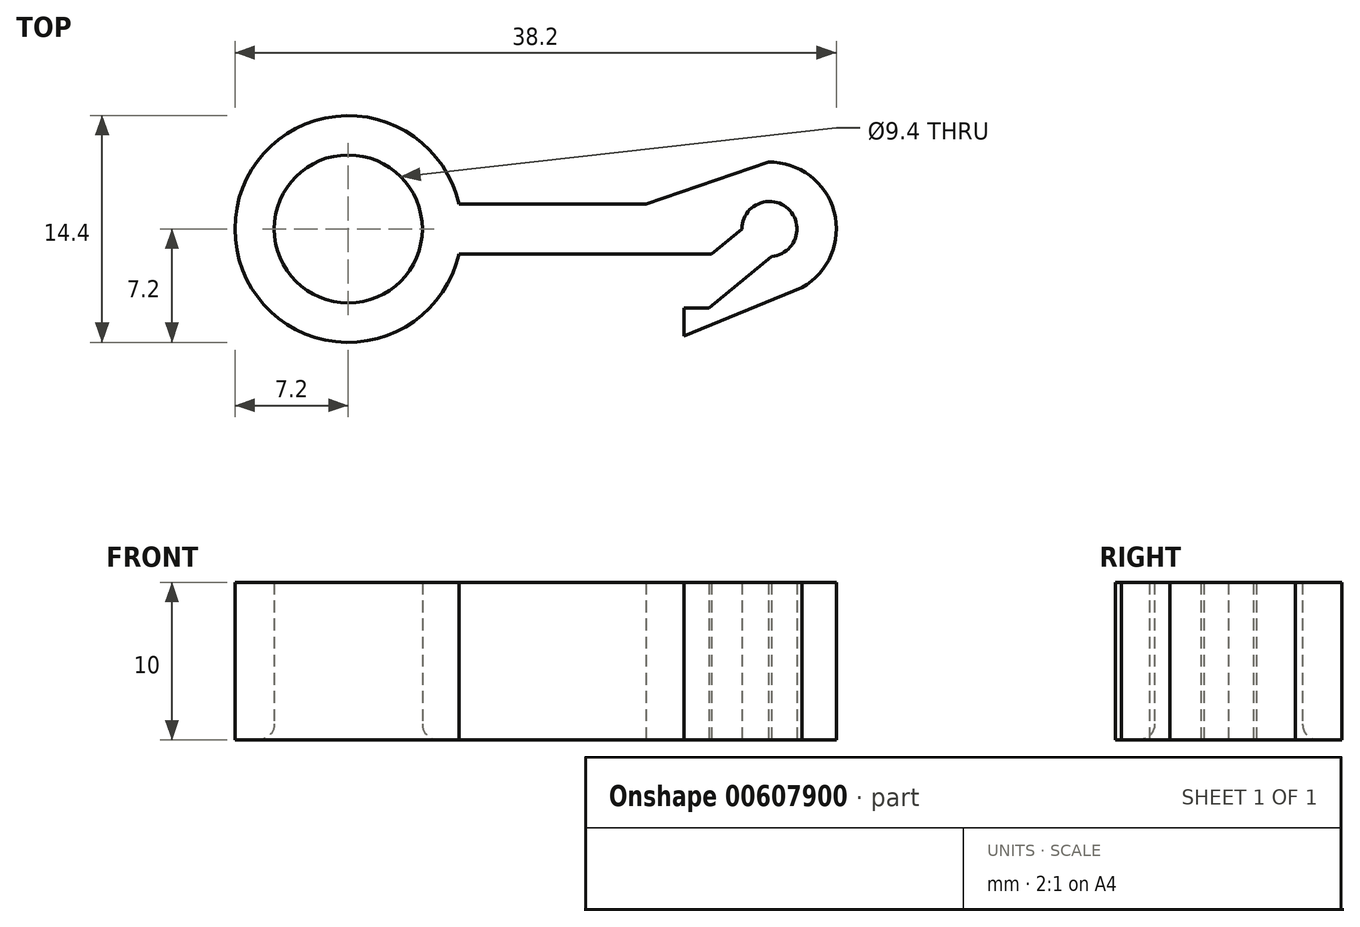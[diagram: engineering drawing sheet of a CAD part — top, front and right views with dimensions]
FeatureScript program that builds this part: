
annotation { "Feature Type Name" : "Feature", "Feature Type Description" : "" }
export const myFeature = defineFeature(function(context is Context, id is Id, definition is map)
    precondition{}
    {
        {
            var Q0;
            Q0=qCreatedBy(makeId("Top.planeOp"),FACE);
            var sketch = newSketch(context, id + "F0", { "sketchPlane" : qUnion([Q0])});
            skCircle(sketch, "E0", {"center": v(0, 0) * mm, "radius": 4.7 * mm});
            skCircle(sketch, "E1", {"center": v(0, 0) * mm, "radius": 7.2 * mm});
            skLineSegment(sketch, "E2.bottom", {"start": v(25, 1.58) * mm, "end": v(-25, 1.58) * mm});
            skLineSegment(sketch, "E2.top", {"start": v(25, -1.58) * mm, "end": v(-25, -1.58) * mm});
            skLineSegment(sketch, "E2.left", {"start": v(25, 1.58) * mm, "end": v(25, -1.58) * mm});
            skLineSegment(sketch, "E2.right", {"start": v(-25, 1.58) * mm, "end": v(-25, -1.58) * mm});
            skCircle(sketch, "E3", {"center": v(26.75, 0) * mm, "radius": 4.25 * mm});
            skCircle(sketch, "E4", {"center": v(26.75, 0) * mm, "radius": 1.75 * mm});
            skLineSegment(sketch, "E5", {"start": v(26.69, 4.25) * mm, "end": v(18.9, 1.58) * mm});
            skLineSegment(sketch, "E6", {"start": v(25, 0) * mm, "end": v(21.76, -2.63) * mm});
            skLineSegment(sketch, "E7", {"start": v(26.88, -1.74) * mm, "end": v(22.9, -5.03) * mm});
            skLineSegment(sketch, "E8", {"start": v(22.9, -5.03) * mm, "end": v(21.32, -5.03) * mm});
            skLineSegment(sketch, "E9", {"start": v(21.32, -5.03) * mm, "end": v(21.32, -6.8) * mm});
            skLineSegment(sketch, "E10", {"start": v(21.32, -6.8) * mm, "end": v(28.82, -3.71) * mm});
            skSolve(sketch);
        }
        {
            var Q0;
            {var subQ0=sQuery(id+"F0.wireOp",EDGE,"E2.bottom");var subQ1=sQuery(id+"F0.wireOp",EDGE,"E0");var subQ2=makeQuery(id+"F0.imprint","INTERSECT",VERTEX,{"disambiguationData":[OD(0.0)],"derivedFrom":[subQ1,subQ0]});Q0=makeQuery(id+"F0.imprint","IMPRINT",FACE,{"disambiguationData":[TD([[makeQuery(id+"F0.imprint","IMPRINT",EDGE,{"disambiguationData":[TD([[subQ2,1.0]])],"derivedFrom":subQ1}),-1.0]])]});}
            var Q1;
            {var subQ0=sQuery(id+"F0.wireOp",EDGE,"E2.bottom");var subQ1=sQuery(id+"F0.wireOp",EDGE,"E0");var subQ2=makeQuery(id+"F0.imprint","INTERSECT",VERTEX,{"disambiguationData":[OD(0.0)],"derivedFrom":[subQ1,subQ0]});Q1=makeQuery(id+"F0.imprint","IMPRINT",FACE,{"disambiguationData":[TD([[makeQuery(id+"F0.imprint","IMPRINT",EDGE,{"disambiguationData":[TD([[subQ2,-1.0]])],"derivedFrom":subQ1}),-1.0]])]});}
            var Q2;
            {var subQ0=sQuery(id+"F0.wireOp",EDGE,"E2.top");var subQ1=sQuery(id+"F0.wireOp",EDGE,"E0");var subQ2=makeQuery(id+"F0.imprint","INTERSECT",VERTEX,{"disambiguationData":[OD(0.0)],"derivedFrom":[subQ1,subQ0]});Q2=makeQuery(id+"F0.imprint","IMPRINT",FACE,{"disambiguationData":[TD([[makeQuery(id+"F0.imprint","IMPRINT",EDGE,{"disambiguationData":[TD([[subQ2,-1.0]])],"derivedFrom":subQ1}),-1.0]])]});}
            var Q3;
            {var subQ0=sQuery(id+"F0.wireOp",EDGE,"E2.bottom");var subQ1=sQuery(id+"F0.wireOp",EDGE,"E0");var subQ2=makeQuery(id+"F0.imprint","INTERSECT",VERTEX,{"disambiguationData":[OD(1.0)],"derivedFrom":[subQ1,subQ0]});Q3=makeQuery(id+"F0.imprint","IMPRINT",FACE,{"disambiguationData":[TD([[makeQuery(id+"F0.imprint","IMPRINT",EDGE,{"disambiguationData":[TD([[subQ2,1.0]])],"derivedFrom":subQ1}),-1.0]])]});}
            var Q4;
            {var subQ0=sQuery(id+"F0.wireOp",EDGE,"5CvTY8nU-JTOH-syRr-r7Hy-UfEV78TZFS7i");Q4=makeQuery(id+"F0.imprint","IMPRINT",FACE,{"disambiguationData":[TD([[makeQuery(id+"F0.imprint","IMPRINT",EDGE,{"derivedFrom":subQ0}),1.0]])]});}
            var Q5;
            {var subQ1=sQuery(id+"F0.wireOp",EDGE,"E2.left");var subQ6=sQuery(id+"F0.wireOp",EDGE,"E2.bottom");var subQ9=makeQuery(id+"F0.imprint","INTERSECT",VERTEX,{"derivedFrom":[subQ6,subQ1]});Q5=makeQuery(id+"F0.imprint","IMPRINT",FACE,{"disambiguationData":[TD([[makeQuery(id+"F0.imprint","IMPRINT",EDGE,{"disambiguationData":[TD([[subQ9,-1.0]])],"derivedFrom":subQ6}),-1.0]])]});}
            var Q6;
            {var subQ3=sQuery(id+"F0.wireOp",EDGE,"E2.bottom");var subQ5=sQuery(id+"F0.wireOp",EDGE,"E2.left");var subQ8=makeQuery(id+"F0.imprint","INTERSECT",VERTEX,{"derivedFrom":[subQ3,subQ5]});Q6=makeQuery(id+"F0.imprint","IMPRINT",FACE,{"disambiguationData":[TD([[makeQuery(id+"F0.imprint","IMPRINT",EDGE,{"disambiguationData":[TD([[subQ8,-1.0]])],"derivedFrom":subQ3}),1.0]])]});}
            var Q7;
            {var subQ0=sQuery(id+"F0.wireOp",EDGE,"E2.bottom");var subQ2=sQuery(id+"F0.wireOp",EDGE,"E1");var subQ3=makeQuery(id+"F0.imprint","INTERSECT",VERTEX,{"disambiguationData":[OD(1.0)],"derivedFrom":[subQ2,subQ0]});Q7=makeQuery(id+"F0.imprint","IMPRINT",FACE,{"disambiguationData":[TD([[makeQuery(id+"F0.imprint","IMPRINT",EDGE,{"disambiguationData":[TD([[subQ3,1.0]])],"derivedFrom":subQ2}),-1.0]])]});}
            var Q8;
            {var subQ0=sQuery(id+"F0.wireOp",EDGE,"E5");var subQ1=sQuery(id+"F0.wireOp",EDGE,"E2.bottom");var subQ2=makeQuery(id+"F0.imprint","INTERSECT",VERTEX,{"derivedFrom":[subQ1,subQ0]});Q8=makeQuery(id+"F0.imprint","IMPRINT",FACE,{"disambiguationData":[TD([[makeQuery(id+"F0.imprint","IMPRINT",EDGE,{"disambiguationData":[TD([[subQ2,1.0]])],"derivedFrom":subQ1}),-1.0]])]});}
            var Q9;
            {var subQ1=sQuery(id+"F0.wireOp",EDGE,"E8");Q9=makeQuery(id+"F0.imprint","IMPRINT",FACE,{"disambiguationData":[TD([[makeQuery(id+"F0.imprint","IMPRINT",EDGE,{"derivedFrom":subQ1}),1.0]])]});}
            extrude(context, id + "F1", {"entities" : qUnion([Q0, Q1, Q2, Q3, Q4, Q5, Q6, Q7, Q8, Q9]), "depth" : 10 * mm, "offsetDistance" : 25 * mm});
        }
        {
            var Q0;
            Q0=makeQuery(id+"F1.opExtrude","CAP_EDGE",EDGE,{"disambiguationData":[OSD([sQuery(id+"F0.wireOp",EDGE,"E0")])],"isStart":true});
            fillet(context, id + "F2", {"entities" : qUnion([Q0]), "radius" : 1 * mm, "tangentPropagation" : true, "allowEdgeOverflow" : false});
        }
    });
